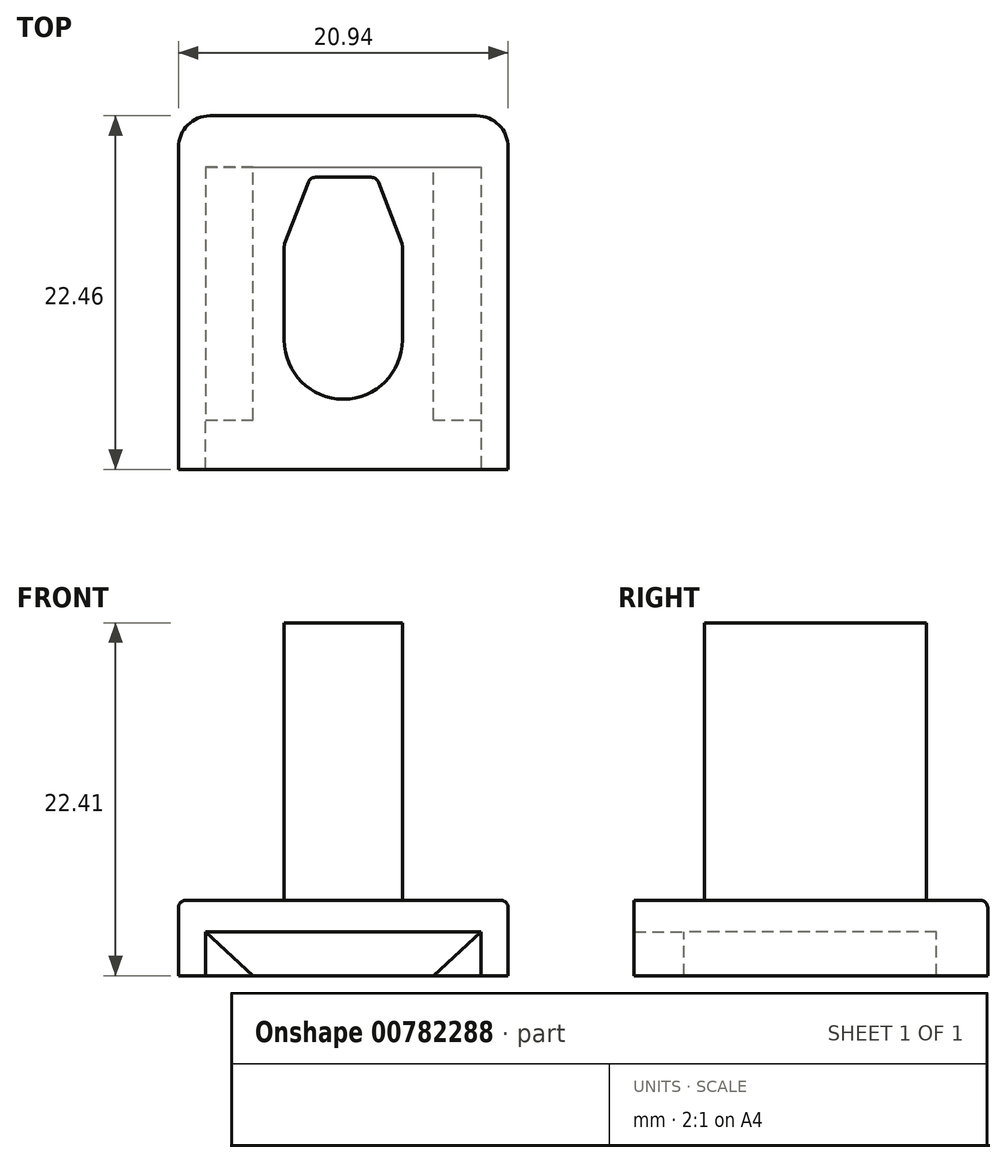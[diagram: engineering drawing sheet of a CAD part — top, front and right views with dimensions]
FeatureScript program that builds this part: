
annotation { "Feature Type Name" : "Feature", "Feature Type Description" : "" }
export const myFeature = defineFeature(function(context is Context, id is Id, definition is map)
    precondition{}
    {
        {
            var Q0;
            Q0=qCreatedBy(makeId("Top.planeOp"),FACE);
            var sketch = newSketch(context, id + "F0", { "sketchPlane" : qUnion([Q0])});
            skLineSegment(sketch, "E0.bottom", {"start": v(8.47, 11.23) * mm, "end": v(-8.47, 11.23) * mm});
            skLineSegment(sketch, "E0.top", {"start": v(10.47, -11.23) * mm, "end": v(-10.47, -11.23) * mm});
            skLineSegment(sketch, "E0.left", {"start": v(10.47, 9.23) * mm, "end": v(10.47, -11.23) * mm});
            skLineSegment(sketch, "E0.right", {"start": v(-10.47, 9.23) * mm, "end": v(-10.47, -11.23) * mm});
            skPoint(sketch, "E0.middle", {"position": v(0, 0) * mm});
            skPoint(sketch, "E1.visualSharp", {"position": v(-10.47, 11.23) * mm});
            skArc(sketch, "E1.filletArc", {"start": v(-8.47, 11.23) * mm, "mid": v(-9.88, 10.64) * mm, "end": v(-10.47, 9.23) * mm});
            skPoint(sketch, "E2.visualSharp", {"position": v(10.47, 11.23) * mm});
            skArc(sketch, "E2.filletArc", {"start": v(10.47, 9.23) * mm, "mid": v(9.88, 10.64) * mm, "end": v(8.47, 11.23) * mm});
            skSolve(sketch);
        }
        {
            var Q0;
            Q0=makeQuery(id+"F0.imprint","IMPRINT",FACE,{"disambiguationData":[TD([[makeQuery(id+"F0.imprint","IMPRINT",EDGE,{"derivedFrom":sQuery(id+"F0.wireOp",EDGE,"E0.bottom")}),1.0]])]});
            extrude(context, id + "F1", {"entities" : qUnion([Q0]), "endBound" : BoundingType.SYMMETRIC, "depth" : 4.8 * mm, "offsetDistance" : 25 * mm});
        }
        {
            var Q0;
            Q0=makeQuery(id+"F1.opExtrude","CAP_FACE",FACE,{"disambiguationData":[OSD([sQuery(id+"F0.wireOp",EDGE,"E0.bottom"),sQuery(id+"F0.wireOp",EDGE,"E0.top"),sQuery(id+"F0.wireOp",EDGE,"E0.left"),sQuery(id+"F0.wireOp",EDGE,"E0.right"),sQuery(id+"F0.wireOp",EDGE,"E1.filletArc"),sQuery(id+"F0.wireOp",EDGE,"E2.filletArc")])],"isStart":false});
            var sketch = newSketch(context, id + "F2", { "sketchPlane" : qUnion([Q0])});
            skLineSegment(sketch, "E3.left", {"start": v(3.75, -3.02) * mm, "end": v(3.75, 3.03) * mm});
            skLineSegment(sketch, "E3.right", {"start": v(-3.75, -3.02) * mm, "end": v(-3.75, 3.03) * mm});
            skPoint(sketch, "E3.middle", {"position": v(0, 0) * mm});
            skArc(sketch, "E4", {"start": v(-3.75, -3.02) * mm, "mid": v(0, -6.77) * mm, "end": v(3.75, -3.02) * mm});
            skLineSegment(sketch, "E5", {"start": v(-3.75, 3.03) * mm, "end": v(-2.1, 7.33) * mm});
            skLineSegment(sketch, "E6", {"start": v(-2.1, 7.33) * mm, "end": v(2.1, 7.33) * mm});
            skLineSegment(sketch, "E7", {"start": v(2.1, 7.33) * mm, "end": v(3.75, 3.03) * mm});
            skSolve(sketch);
        }
        {
            var Q0;
            Q0=makeQuery(id+"F2.imprint","IMPRINT",FACE,{"disambiguationData":[TD([[makeQuery(id+"F2.imprint","IMPRINT",EDGE,{"derivedFrom":sQuery(id+"F2.wireOp",EDGE,"E3.left")}),1.0]])]});
            extrude(context, id + "F3", {"entities" : qUnion([Q0]), "operationType" : NewBodyOperationType.ADD, "depth" : 17.6 * mm, "offsetDistance" : 25 * mm});
        }
        {
            var Q0;
            Q0=makeQuery(id+"F1.opExtrude","CAP_FACE",FACE,{"disambiguationData":[OSD([sQuery(id+"F0.wireOp",EDGE,"E0.bottom"),sQuery(id+"F0.wireOp",EDGE,"E0.top"),sQuery(id+"F0.wireOp",EDGE,"E0.left"),sQuery(id+"F0.wireOp",EDGE,"E0.right"),sQuery(id+"F0.wireOp",EDGE,"E1.filletArc"),sQuery(id+"F0.wireOp",EDGE,"E2.filletArc")])],"isStart":true});
            var sketch = newSketch(context, id + "F4", { "sketchPlane" : qUnion([Q0])});
            skLineSegment(sketch, "E8.top", {"start": v(-5.72, -7.98) * mm, "end": v(5.72, -7.98) * mm});
            skLineSegment(sketch, "E8.left", {"start": v(-5.72, 8.08) * mm, "end": v(-5.72, -7.98) * mm});
            skLineSegment(sketch, "E8.right", {"start": v(5.72, 8.08) * mm, "end": v(5.72, -7.98) * mm});
            skLineSegment(sketch, "E9.left", {"start": v(-8.75, 11.23) * mm, "end": v(-8.75, 8.08) * mm});
            skLineSegment(sketch, "E10", {"start": v(-8.75, 11.23) * mm, "end": v(8.75, 11.23) * mm});
            skLineSegment(sketch, "E11", {"start": v(-8.75, 8.08) * mm, "end": v(-5.72, 8.08) * mm});
            skLineSegment(sketch, "E12", {"start": v(5.72, 8.08) * mm, "end": v(8.75, 8.08) * mm});
            skLineSegment(sketch, "E13", {"start": v(8.75, 8.08) * mm, "end": v(8.75, 11.23) * mm});
            skSolve(sketch);
        }
        {
            var Q0;
            Q0=makeQuery(id+"F4.imprint","IMPRINT",FACE,{"disambiguationData":[TD([[makeQuery(id+"F4.imprint","IMPRINT",EDGE,{"derivedFrom":sQuery(id+"F4.wireOp",EDGE,"E8.top")}),1.0]])]});
            extrude(context, id + "F5", {"entities" : qUnion([Q0]), "operationType" : NewBodyOperationType.REMOVE, "oppositeDirection" : true, "depth" : 2.8 * mm, "offsetDistance" : 25 * mm});
        }
        {
            var Q0;
            Q0=makeQuery(id+"F5.boolean.opBoolean","COPY",FACE,{"derivedFrom":makeQuery(id+"F5.opExtrude","SWEPT_FACE",FACE,{"disambiguationData":[OSD([sQuery(id+"F4.wireOp",EDGE,"E11")])]})});
            var sketch = newSketch(context, id + "F6", { "sketchPlane" : qUnion([Q0])});
            skLineSegment(sketch, "E14", {"start": v(-5.72, -2.4) * mm, "end": v(-8.75, 0.4) * mm});
            skLineSegment(sketch, "E15", {"start": v(-8.75, 0.4) * mm, "end": v(-5.72, 0.4) * mm});
            skLineSegment(sketch, "E16", {"start": v(-5.72, 0.4) * mm, "end": v(-5.72, -2.4) * mm});
            skLineSegment(sketch, "E17.MirrorCS", {"start": v(8.75, 0.4) * mm, "end": v(5.72, 0.4) * mm});
            skLineSegment(sketch, "E18.MirrorCS", {"start": v(5.72, -2.4) * mm, "end": v(8.75, 0.4) * mm});
            skLineSegment(sketch, "E19.MirrorCS", {"start": v(5.72, 0.4) * mm, "end": v(5.72, -2.4) * mm});
            skSolve(sketch);
        }
        {
            var Q0;
            Q0 = qSketchRegion(id + "F6", true);
            var Q1;
            Q1=makeQuery(id+"F5.boolean.opBoolean","COPY",FACE,{"derivedFrom":makeQuery(id+"F5.opExtrude","SWEPT_FACE",FACE,{"disambiguationData":[OSD([sQuery(id+"F4.wireOp",EDGE,"E8.top")])]})});
            extrude(context, id + "F7", {"entities" : qUnion([Q0]), "operationType" : NewBodyOperationType.REMOVE, "endBound" : BoundingType.UP_TO_SURFACE, "oppositeDirection" : true, "depth" : 25 * mm, "endBoundEntityFace" : qUnion([Q1]), "offsetDistance" : 25 * mm});
        }
        {
            var Q0;
            Q0=makeQuery(id+"F1.opExtrude","CAP_EDGE",EDGE,{"disambiguationData":[OSD([sQuery(id+"F0.wireOp",EDGE,"E0.left")])],"isStart":false});
            var Q1;
            Q1=makeQuery(id+"F3.opExtrude","SWEPT_EDGE",EDGE,{"disambiguationData":[OSD([sQuery(id+"F2.wireOp",EDGE,"E3.left"),sQuery(id+"F2.wireOp",EDGE,"E7")])]});
            var Q2;
            Q2=makeQuery(id+"F3.opExtrude","SWEPT_EDGE",EDGE,{"disambiguationData":[OSD([sQuery(id+"F2.wireOp",EDGE,"E3.right"),sQuery(id+"F2.wireOp",EDGE,"E5")])]});
            var Q3;
            Q3=makeQuery(id+"F3.opExtrude","SWEPT_EDGE",EDGE,{"disambiguationData":[OSD([sQuery(id+"F2.wireOp",EDGE,"E5"),sQuery(id+"F2.wireOp",EDGE,"E6")])]});
            var Q4;
            Q4=makeQuery(id+"F3.opExtrude","SWEPT_EDGE",EDGE,{"disambiguationData":[OSD([sQuery(id+"F2.wireOp",EDGE,"E6"),sQuery(id+"F2.wireOp",EDGE,"E7")])]});
            var Q5;
            Q5=makeQuery(id+"F3.opExtrude","CAP_EDGE",EDGE,{"disambiguationData":[OSD([sQuery(id+"F2.wireOp",EDGE,"E4")])],"isStart":true});
            fillet(context, id + "F8", {"entities" : qUnion([Q0, Q1, Q2, Q3, Q4, Q5]), "radius" : .5 * mm, "tangentPropagation" : true, "allowEdgeOverflow" : false});
        }
    });
